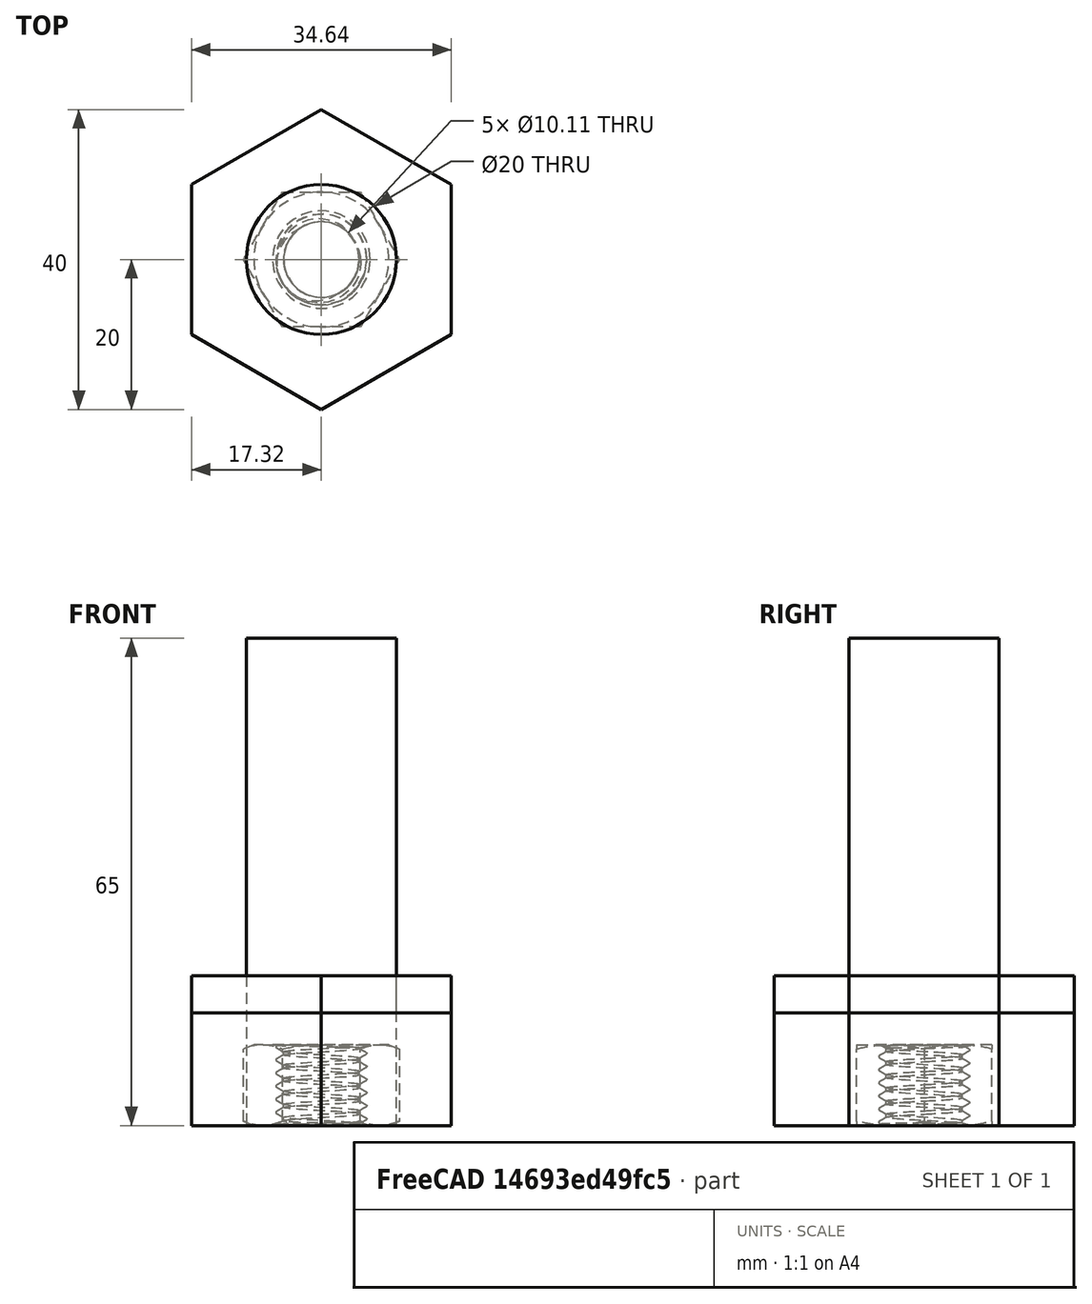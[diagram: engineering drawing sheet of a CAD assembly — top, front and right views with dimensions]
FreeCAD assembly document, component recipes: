
FREECAD ASSEMBLY — COMPONENT RECIPES ("Unnamed")

This assembly document has 2 components, labeled P0..P1 below (a component is one placed body or linked part). 2 of them carry a construction recipe — the FreeCAD feature program that regenerates the part from scratch, quoted from this document or its linked companion documents; the rest are supplied as boundary geometry only. No exploded tour is included for this assembly.
COMPONENT P0 — recipe-attached ("BoltBody001", modeled in this document).
Construction recipe (the document's own serialized feature program — sketch geometry with constraints, then the solid features built on it; lengths are millimeters unless a unit is written):

FEATURE [Sketcher::SketchObject] Sketch004
  ArcFitTolerance = 1e-06
  AttachmentSupport = -> [XY_Plane001]
  FullyConstrained = true
  MakeInternals = false
  MapMode = 5
  sketch-geometry (7):
    g0: LineSegment StartX=0 StartY=20 StartZ=0 EndX=-17.3205 EndY=10 EndZ=0
    g1: LineSegment StartX=-17.3205 StartY=10 StartZ=0 EndX=-17.3205 EndY=-10 EndZ=0
    g2: LineSegment StartX=-17.3205 StartY=-10 StartZ=0 EndX=0 EndY=-20 EndZ=0
    g3: LineSegment StartX=0 StartY=-20 StartZ=0 EndX=17.3205 EndY=-10 EndZ=0
    g4: LineSegment StartX=17.3205 StartY=-10 StartZ=0 EndX=17.3205 EndY=10 EndZ=0
    g5: LineSegment StartX=17.3205 StartY=10 StartZ=0 EndX=0 EndY=20 EndZ=0
    g6: Circle [constr] CenterX=0 CenterY=0 CenterZ=0 NormalX=0 NormalY=0 NormalZ=1 AngleXU=0 Radius=20
  constraints (16):
    c: Coincident(g0,g1)
    c: Coincident(g1,g2)
    c: Coincident(g2,g3)
    c: Coincident(g3,g4)
    c: Coincident(g4,g5)
    c: Coincident(g5,g0)
    c: Equal(g0, g1-g5) x5
    c: PointOnObject(g0,g6)
    c: PointOnObject(g1,g6)
    c: PointOnObject(g2,g6)
    c: PointOnObject(g3,g6)
    c: PointOnObject(g4,g6)
    c: PointOnObject(g5,g6)
    c: Coincident(g6,g-1)
    c: PointOnObject(g5,g-2)
    c: Distance(g0,g3) = 40
FEATURE [PartDesign::Pad] Pad001
  Direction = (0,0,1)
  Length = 15
  Length2 = 10
  Profile = -> Sketch004
  ReferenceAxis = -> Sketch004 [N_Axis]
  Refine = true
  Suppressed = false
  Type = 0
FEATURE [Sketcher::SketchObject] Sketch005
  ArcFitTolerance = 1e-06
  AttachmentSupport = -> [Pad001]
  FullyConstrained = true
  MakeInternals = false
  MapMode = 5
  Placement = pos=(0,0,15) rot=(0,0,1;0rad)
  sketch-geometry (1):
    g0: Circle CenterX=0 CenterY=0 CenterZ=0 NormalX=0 NormalY=0 NormalZ=1 AngleXU=0 Radius=10
  constraints (2):
    c: Diameter(g0) = 20
    c: Coincident(g0,g-1)
FEATURE [PartDesign::Pad] Pad002
  BaseFeature = -> Pad001
  Direction = (0,0,1)
  Length = 50
  Length2 = 10
  Profile = -> Sketch005 [Edge1]
  ReferenceAxis = -> Sketch005 [N_Axis]
  Refine = true
  Suppressed = false
  Type = 0
FEATURE [PartDesign::Body] Body001  label="BoltBody"
  AllowCompound = false
  Group = -> [Sketch004,Pad001,Sketch005,Pad002]
  Origin = -> Origin001
  Tip = -> Pad002
COMPONENT P1 — recipe-attached ("NutBody001", modeled in this document).
Construction recipe (the document's own serialized feature program — sketch geometry with constraints, then the solid features built on it; lengths are millimeters unless a unit is written):

FEATURE [Sketcher::SketchObject] Sketch
  ArcFitTolerance = 1e-06
  AttachmentSupport = -> [XY_Plane]
  FullyConstrained = true
  MakeInternals = false
  MapMode = 5
  sketch-geometry (8):
    g0: LineSegment StartX=0 StartY=20 StartZ=0 EndX=-17.3205 EndY=10 EndZ=0
    g1: LineSegment StartX=-17.3205 StartY=10 StartZ=0 EndX=-17.3205 EndY=-10 EndZ=0
    g2: LineSegment StartX=-17.3205 StartY=-10 StartZ=0 EndX=-3.6e-15 EndY=-20 EndZ=0
    g3: LineSegment StartX=-3.6e-15 StartY=-20 StartZ=0 EndX=17.3205 EndY=-10 EndZ=0
    g4: LineSegment StartX=17.3205 StartY=-10 StartZ=0 EndX=17.3205 EndY=10 EndZ=0
    g5: LineSegment StartX=17.3205 StartY=10 StartZ=0 EndX=0 EndY=20 EndZ=0
    g6: Circle [constr] CenterX=0 CenterY=0 CenterZ=0 NormalX=0 NormalY=0 NormalZ=1 AngleXU=0 Radius=20
    g7: Circle CenterX=0 CenterY=0 CenterZ=0 NormalX=0 NormalY=0 NormalZ=1 AngleXU=0 Radius=10
  constraints (18):
    c: Coincident(g0,g1)
    c: Coincident(g1,g2)
    c: Coincident(g2,g3)
    c: Coincident(g3,g4)
    c: Coincident(g4,g5)
    c: Coincident(g5,g0)
    c: Equal(g0, g1-g5) x5
    c: PointOnObject(g0,g6)
    c: PointOnObject(g1,g6)
    c: PointOnObject(g2,g6)
    c: PointOnObject(g3,g6)
    c: PointOnObject(g4,g6)
    c: PointOnObject(g5,g6)
    c: Coincident(g6,g-1)
    c: PointOnObject(g5,g-2)
    c: Diameter(g7) = 20
    c: Coincident(g7,g6)
    c: DistanceY(g2,g0) = 40
FEATURE [PartDesign::Pad] Pad
  Direction = (0,0,1)
  Length = 20
  Length2 = 10
  Profile = -> Sketch
  ReferenceAxis = -> Sketch [N_Axis]
  Refine = true
  Suppressed = false
  Type = 0
FEATURE [PartDesign::Body] Body  label="NutBody"
  AllowCompound = false
  Group = -> [Sketch,Pad]
  Origin = -> Origin
  Tip = -> Pad
PROVENANCE & LICENSES
A FreeCAD (.FCStd) document from a public repository crawl; recipes are the document's own serialized feature recipes (and, for linked parts, companion documents' recipes).
License: mit.
